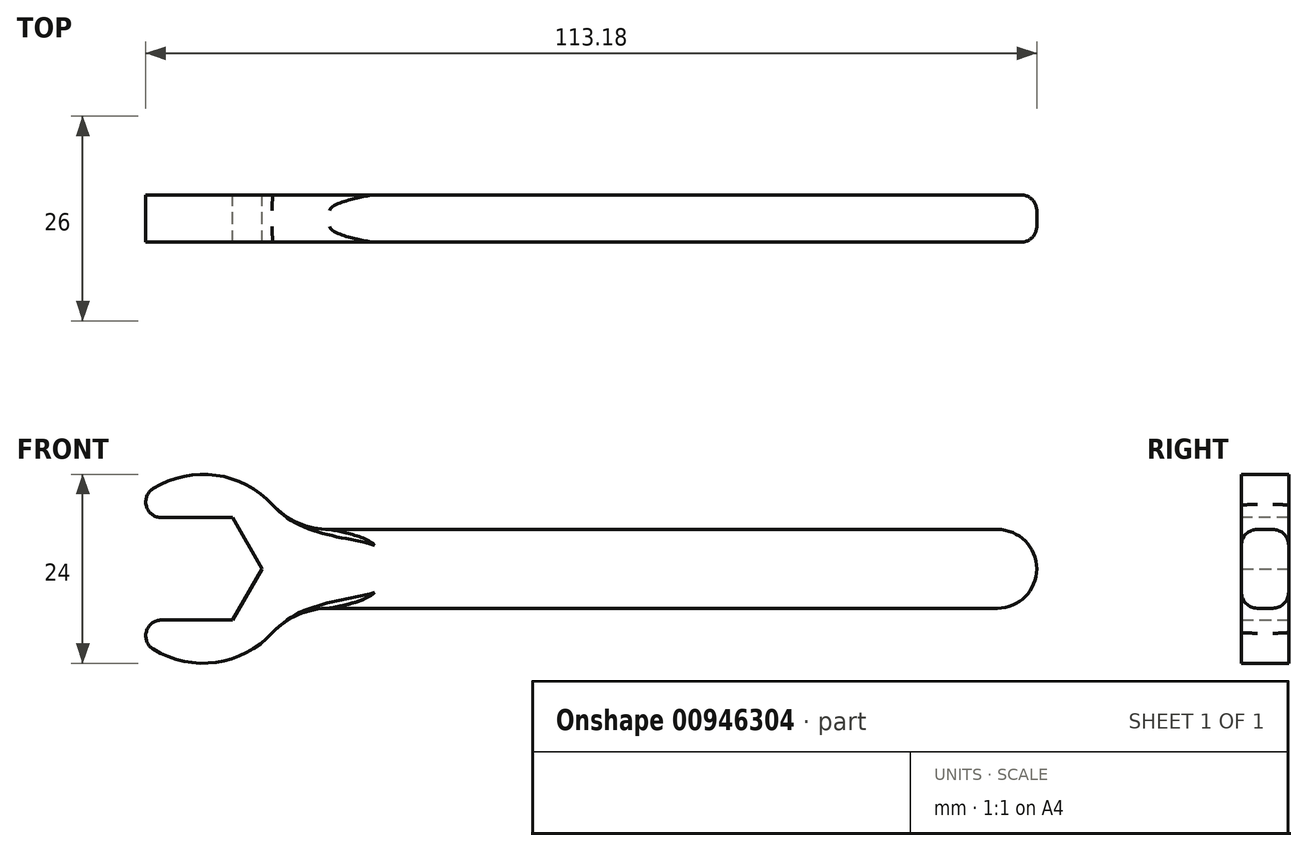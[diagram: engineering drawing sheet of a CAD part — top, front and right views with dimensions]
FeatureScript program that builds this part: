
annotation { "Feature Type Name" : "Feature", "Feature Type Description" : "" }
export const myFeature = defineFeature(function(context is Context, id is Id, definition is map)
    precondition{}
    {
        {
            var Q0;
            Q0=qCreatedBy(makeId("Front.planeOp"),FACE);
            var sketch = newSketch(context, id + "F0", { "sketchPlane" : qUnion([Q0])});
            skArc(sketch, "E0", {"start": v(-10.09, -6.5) * mm, "mid": v(12, 0) * mm, "end": v(-10.09, 6.5) * mm});
            skCircle(sketch, "E1.cCircle", {"center": v(0, 0) * mm, "radius": 6.5 * mm, "construction": true});
            skLineSegment(sketch, "E1.0", {"start": v(-3.75, 6.5) * mm, "end": v(3.75, 6.5) * mm});
            skLineSegment(sketch, "E1.1", {"start": v(3.75, 6.5) * mm, "end": v(7.5, 0) * mm});
            skLineSegment(sketch, "E1.2", {"start": v(7.5, 0) * mm, "end": v(3.75, -6.5) * mm});
            skLineSegment(sketch, "E1.3", {"start": v(3.75, -6.5) * mm, "end": v(-3.75, -6.5) * mm});
            skPoint(sketch, "E1.0.midPoint", {"position": v(0, 6.5) * mm});
            skLineSegment(sketch, "E2.bottom", {"start": v(10.9, 5) * mm, "end": v(105.9, 5) * mm});
            skLineSegment(sketch, "E2.top", {"start": v(10.9, -5) * mm, "end": v(105.9, -5) * mm});
            skLineSegment(sketch, "E2.left", {"start": v(10.9, 5) * mm, "end": v(10.9, -5) * mm});
            skLineSegment(sketch, "E2.right", {"start": v(105.9, 5) * mm, "end": v(105.9, -5) * mm});
            skLineSegment(sketch, "E3", {"start": v(-3.75, 6.5) * mm, "end": v(-10.09, 6.5) * mm});
            skLineSegment(sketch, "E4", {"start": v(-3.75, -6.5) * mm, "end": v(-10.09, -6.5) * mm});
            skSolve(sketch);
        }
        {
            var Q0;
            Q0=makeQuery(id+"F0.imprint","IMPRINT",FACE,{"disambiguationData":[TD([[makeQuery(id+"F0.imprint","IMPRINT",EDGE,{"derivedFrom":sQuery(id+"F0.wireOp",EDGE,"E1.0")}),1.0]])]});
            var Q1;
            {var subQ0=sQuery(id+"F0.wireOp",EDGE,"E2.left");Q1=makeQuery(id+"F0.imprint","IMPRINT",FACE,{"disambiguationData":[TD([[makeQuery(id+"F0.imprint","IMPRINT",EDGE,{"derivedFrom":subQ0}),1.0]])]});}
            var Q2;
            {var subQ1=sQuery(id+"F0.wireOp",EDGE,"E2.bottom");Q2=makeQuery(id+"F0.imprint","IMPRINT",FACE,{"disambiguationData":[TD([[makeQuery(id+"F0.imprint","IMPRINT",EDGE,{"derivedFrom":subQ1}),-1.0]])]});}
            extrude(context, id + "F1", {"entities" : qUnion([Q0, Q1, Q2]), "depth" : 6 * mm, "offsetDistance" : 25 * mm});
        }
        {
            var Q0;
            Q0=makeQuery(id+"F1.opExtrude","SWEPT_EDGE",EDGE,{"disambiguationData":[OSD([sQuery(id+"F0.wireOp",EDGE,"E0"),sQuery(id+"F0.wireOp",EDGE,"E3")])]});
            var Q1;
            Q1=makeQuery(id+"F1.opExtrude","SWEPT_EDGE",EDGE,{"disambiguationData":[OSD([sQuery(id+"F0.wireOp",EDGE,"E0"),sQuery(id+"F0.wireOp",EDGE,"E4")])]});
            fillet(context, id + "F2", {"entities" : qUnion([Q0, Q1]), "radius" : 2 * mm, "tangentPropagation" : true, "allowEdgeOverflow" : false});
        }
        {
            var Q0;
            Q0=makeQuery(id+"F1.opExtrude","SWEPT_EDGE",EDGE,{"disambiguationData":[OSD([sQuery(id+"F0.wireOp",EDGE,"E2.bottom"),sQuery(id+"F0.wireOp",EDGE,"E2.right")])]});
            var Q1;
            Q1=makeQuery(id+"F1.opExtrude","SWEPT_EDGE",EDGE,{"disambiguationData":[OSD([sQuery(id+"F0.wireOp",EDGE,"E2.top"),sQuery(id+"F0.wireOp",EDGE,"E2.right")])]});
            fillet(context, id + "F3", {"entities" : qUnion([Q0, Q1]), "radius" : 5 * mm, "tangentPropagation" : true, "allowEdgeOverflow" : false});
        }
        {
            var Q0;
            Q0=makeQuery(id+"F1.opExtrude","CAP_EDGE",EDGE,{"disambiguationData":[OSD([sQuery(id+"F0.wireOp",EDGE,"E2.bottom")])],"isStart":true});
            var Q1;
            Q1=makeQuery(id+"F1.opExtrude","CAP_EDGE",EDGE,{"disambiguationData":[OSD([sQuery(id+"F0.wireOp",EDGE,"E2.bottom")])],"isStart":false});
            fillet(context, id + "F4", {"entities" : qUnion([Q0, Q1]), "radius" : 2 * mm, "tangentPropagation" : true, "allowEdgeOverflow" : false});
        }
        {
            var Q0;
            Q0=makeQuery(id+"F1.opExtrude","SWEPT_EDGE",EDGE,{"disambiguationData":[OSD([sQuery(id+"F0.wireOp",EDGE,"E0"),sQuery(id+"F0.wireOp",EDGE,"E2.top"),sQuery(id+"F0.wireOp",EDGE,"E2.left")])]});
            var Q1;
            Q1=makeQuery(id+"F1.opExtrude","SWEPT_EDGE",EDGE,{"disambiguationData":[OSD([sQuery(id+"F0.wireOp",EDGE,"E0"),sQuery(id+"F0.wireOp",EDGE,"E2.bottom"),sQuery(id+"F0.wireOp",EDGE,"E2.left")])]});
            fillet(context, id + "F5", {"entities" : qUnion([Q0, Q1]), "radius" : 10 * mm, "tangentPropagation" : true, "allowEdgeOverflow" : false});
        }
    });
